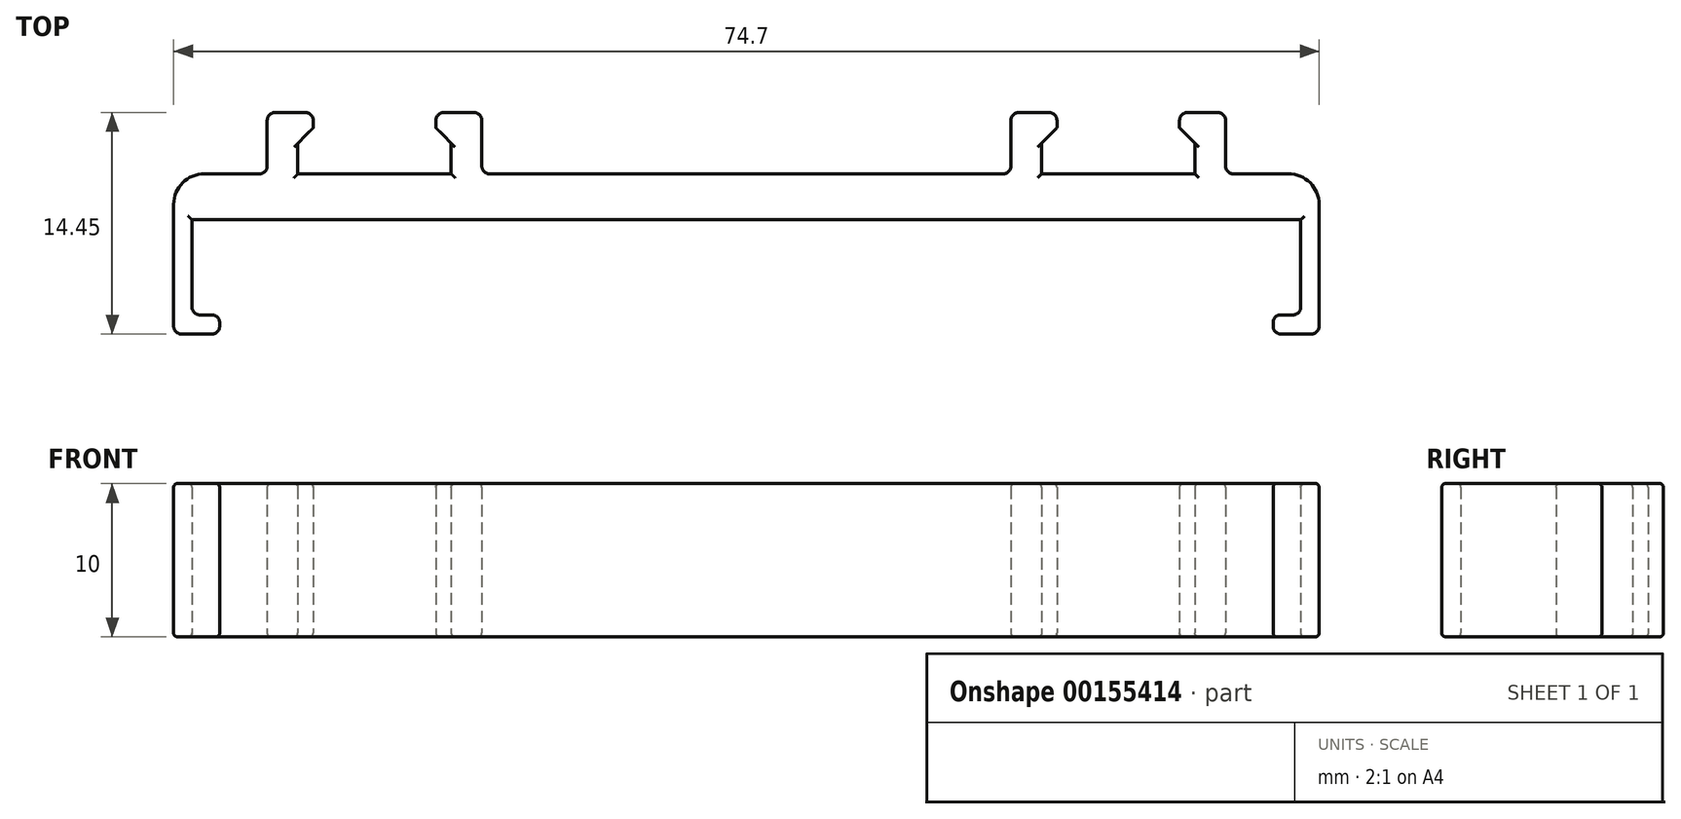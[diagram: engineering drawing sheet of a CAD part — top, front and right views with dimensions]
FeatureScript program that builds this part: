
annotation { "Feature Type Name" : "Feature", "Feature Type Description" : "" }
export const myFeature = defineFeature(function(context is Context, id is Id, definition is map)
    precondition{}
    {
        {
            var Q0;
            Q0=qCreatedBy(makeId("Top.planeOp"),FACE);
            var sketch = newSketch(context, id + "F0", { "sketchPlane" : qUnion([Q0])});
            skLineSegment(sketch, "E0.bottom", {"start": v(-35.35, 3) * mm, "end": v(-31.75, 3) * mm});
            skLineSegment(sketch, "E0.top", {"start": v(-36.15, 0) * mm, "end": v(0, 0) * mm});
            skLineSegment(sketch, "E0.left", {"start": v(-37.35, 1) * mm, "end": v(-37.35, -6.95) * mm});
            skLineSegment(sketch, "E0.right", {"start": v(0, 3) * mm, "end": v(0, 0) * mm});
            skLineSegment(sketch, "E1", {"start": v(-36.85, -7.45) * mm, "end": v(-34.85, -7.45) * mm});
            skLineSegment(sketch, "E2", {"start": v(-31.25, 3.5) * mm, "end": v(-31.25, 6.5) * mm});
            skLineSegment(sketch, "E3", {"start": v(-29.25, 5) * mm, "end": v(-29.25, 3) * mm});
            skLineSegment(sketch, "E4", {"start": v(-19.25, 3) * mm, "end": v(-19.25, 5) * mm});
            skLineSegment(sketch, "E5", {"start": v(-17.25, 6.5) * mm, "end": v(-17.25, 3.5) * mm});
            skLineSegment(sketch, "E6.trimOffspring", {"start": v(-29.25, 3) * mm, "end": v(-19.25, 3) * mm});
            skLineSegment(sketch, "E7.trimOffspring", {"start": v(-16.75, 3) * mm, "end": v(0, 3) * mm});
            skLineSegment(sketch, "E8", {"start": v(-30.75, 7) * mm, "end": v(-28.75, 7) * mm});
            skLineSegment(sketch, "E9", {"start": v(-28.25, 6.5) * mm, "end": v(-28.25, 6) * mm});
            skLineSegment(sketch, "E10", {"start": v(-19.75, 7) * mm, "end": v(-17.75, 7) * mm});
            skPoint(sketch, "E11.visualSharp", {"position": v(-37.35, 3) * mm});
            skArc(sketch, "E11.filletArc", {"start": v(-35.35, 3) * mm, "mid": v(-36.76, 2.41) * mm, "end": v(-37.35, 1) * mm});
            skPoint(sketch, "E12.visualSharp", {"position": v(-37.35, -7.45) * mm});
            skArc(sketch, "E12.filletArc", {"start": v(-37.35, -6.95) * mm, "mid": v(-37.2, -7.3) * mm, "end": v(-36.85, -7.45) * mm});
            skArc(sketch, "E13.filletArc", {"start": v(-28.25, 6.5) * mm, "mid": v(-28.4, 6.85) * mm, "end": v(-28.75, 7) * mm});
            skPoint(sketch, "E14.visualSharp", {"position": v(-31.25, 7) * mm});
            skArc(sketch, "E14.filletArc", {"start": v(-30.75, 7) * mm, "mid": v(-31.1, 6.85) * mm, "end": v(-31.25, 6.5) * mm});
            skArc(sketch, "E15.filletArc", {"start": v(-17.25, 6.5) * mm, "mid": v(-17.4, 6.85) * mm, "end": v(-17.75, 7) * mm});
            skArc(sketch, "E16.filletArc", {"start": v(-19.75, 7) * mm, "mid": v(-20.1, 6.85) * mm, "end": v(-20.25, 6.5) * mm});
            skPoint(sketch, "E17.visualSharp", {"position": v(-31.25, 3) * mm});
            skArc(sketch, "E17.filletArc", {"start": v(-31.75, 3) * mm, "mid": v(-31.4, 3.15) * mm, "end": v(-31.25, 3.5) * mm});
            skPoint(sketch, "E18.visualSharp", {"position": v(-17.25, 3) * mm});
            skArc(sketch, "E18.filletArc", {"start": v(-17.25, 3.5) * mm, "mid": v(-17.1, 3.15) * mm, "end": v(-16.75, 3) * mm});
            skLineSegment(sketch, "E19", {"start": v(-34.35, -6.95) * mm, "end": v(-34.35, -6.7) * mm});
            skLineSegment(sketch, "E20", {"start": v(-34.85, -6.2) * mm, "end": v(-35.65, -6.2) * mm});
            skLineSegment(sketch, "E21", {"start": v(-36.15, -5.7) * mm, "end": v(-36.15, 0) * mm});
            skPoint(sketch, "E22.visualSharp", {"position": v(-34.35, -7.45) * mm});
            skArc(sketch, "E22.filletArc", {"start": v(-34.85, -7.45) * mm, "mid": v(-34.5, -7.3) * mm, "end": v(-34.35, -6.95) * mm});
            skPoint(sketch, "E23.visualSharp", {"position": v(-34.35, -6.2) * mm});
            skArc(sketch, "E23.filletArc", {"start": v(-34.35, -6.7) * mm, "mid": v(-34.5, -6.35) * mm, "end": v(-34.85, -6.2) * mm});
            skPoint(sketch, "E24.visualSharp", {"position": v(-36.15, -6.2) * mm});
            skArc(sketch, "E24.filletArc", {"start": v(-36.15, -5.7) * mm, "mid": v(-36, -6.05) * mm, "end": v(-35.65, -6.2) * mm});
            skLineSegment(sketch, "E25", {"start": v(-29.25, 5) * mm, "end": v(-28.25, 6) * mm});
            skLineSegment(sketch, "E26", {"start": v(-29.25, 5) * mm, "end": v(-26.76, 5) * mm, "construction": true});
            skLineSegment(sketch, "E27", {"start": v(-20.25, 6.5) * mm, "end": v(-20.25, 6) * mm});
            skLineSegment(sketch, "E28", {"start": v(-20.25, 6) * mm, "end": v(-19.25, 5) * mm});
            skLineSegment(sketch, "E29", {"start": v(-19.25, 5) * mm, "end": v(-20.65, 5) * mm, "construction": true});
            skSolve(sketch);
        }
        {
            var Q0;
            Q0 = qSketchRegion(id + "F0", true);
            extrude(context, id + "F1", {"entities" : qUnion([Q0]), "depth" : 5 * mm});
        }
        {
            var Q0;
            Q0=makeQuery(id+"F1.opExtrude","CAP_EDGE",EDGE,{"disambiguationData":[OSD([sQuery(id+"F0.wireOp",EDGE,"E0.left")])],"isStart":false});
            var Q1;
            Q1=makeQuery(id+"F1.opExtrude","CAP_EDGE",EDGE,{"disambiguationData":[OSD([sQuery(id+"F0.wireOp",EDGE,"tvZSsmSE-hUvE-Xtk3-tDF4-9MUb7sZ0VrVc")])],"isStart":false});
            var Q2;
            Q2=makeQuery(id+"F1.opExtrude","CAP_EDGE",EDGE,{"disambiguationData":[OSD([sQuery(id+"F0.wireOp",EDGE,"E0.top")])],"isStart":false});
            var Q3;
            Q3=makeQuery(id+"F1.opExtrude","CAP_EDGE",EDGE,{"disambiguationData":[OSD([sQuery(id+"F0.wireOp",EDGE,"E7.trimOffspring")])],"isStart":false});
            var Q4;
            Q4=makeQuery(id+"F1.opExtrude","CAP_EDGE",EDGE,{"disambiguationData":[OSD([sQuery(id+"F0.wireOp",EDGE,"X6ObSeEj-YZr1-teH5-AZXu-cSIaNaP9HJV4")])],"isStart":false});
            var Q5;
            Q5=makeQuery(id+"F1.opExtrude","CAP_EDGE",EDGE,{"disambiguationData":[OSD([sQuery(id+"F0.wireOp",EDGE,"E4")])],"isStart":false});
            var Q6;
            Q6=makeQuery(id+"F1.opExtrude","CAP_EDGE",EDGE,{"disambiguationData":[OSD([sQuery(id+"F0.wireOp",EDGE,"E6.trimOffspring")])],"isStart":false});
            var Q7;
            Q7=makeQuery(id+"F1.opExtrude","CAP_EDGE",EDGE,{"disambiguationData":[OSD([sQuery(id+"F0.wireOp",EDGE,"E3")])],"isStart":false});
            var Q8;
            Q8=makeQuery(id+"F1.opExtrude","CAP_EDGE",EDGE,{"disambiguationData":[OSD([sQuery(id+"F0.wireOp",EDGE,"p37QHmaa-qxUZ-rcvS-T9Jj-RTMhVuBpOhlm")])],"isStart":false});
            fillet(context, id + "F2", {"entities" : qUnion([Q0, Q1, Q2, Q3, Q4, Q5, Q6, Q7, Q8]), "radius" : 0.25 * mm, "tangentPropagation" : true, "allowEdgeOverflow" : false});
        }
        {
            var Q0;
            Q0=makeQuery(id+"F1.opExtrude","SWEPT_BODY",BODY,{"disambiguationData":[OSD([sQuery(id+"F0.wireOp",EDGE,"E0.bottom"),sQuery(id+"F0.wireOp",EDGE,"E0.top"),sQuery(id+"F0.wireOp",EDGE,"E0.left"),sQuery(id+"F0.wireOp",EDGE,"E0.right"),sQuery(id+"F0.wireOp",EDGE,"E1"),sQuery(id+"F0.wireOp",EDGE,"hb15ITHf-txwg-p7V1-AkCO-Q5CLrczJ6zII"),sQuery(id+"F0.wireOp",EDGE,"Mp94Wzwl-Bjus-MnSt-C4gq-dxj1KtEF7oJ2"),sQuery(id+"F0.wireOp",EDGE,"tvZSsmSE-hUvE-Xtk3-tDF4-9MUb7sZ0VrVc"),sQuery(id+"F0.wireOp",EDGE,"E2"),sQuery(id+"F0.wireOp",EDGE,"p37QHmaa-qxUZ-rcvS-T9Jj-RTMhVuBpOhlm"),sQuery(id+"F0.wireOp",EDGE,"E3"),sQuery(id+"F0.wireOp",EDGE,"E4"),sQuery(id+"F0.wireOp",EDGE,"X6ObSeEj-YZr1-teH5-AZXu-cSIaNaP9HJV4"),sQuery(id+"F0.wireOp",EDGE,"E5"),sQuery(id+"F0.wireOp",EDGE,"E6.trimOffspring"),sQuery(id+"F0.wireOp",EDGE,"E7.trimOffspring"),sQuery(id+"F0.wireOp",EDGE,"E8"),sQuery(id+"F0.wireOp",EDGE,"E9"),sQuery(id+"F0.wireOp",EDGE,"iGBChI1A-pXvF-3BVJ-ZSPA-OomGo4UHPv9J"),sQuery(id+"F0.wireOp",EDGE,"E10"),sQuery(id+"F0.wireOp",EDGE,"E11.filletArc"),sQuery(id+"F0.wireOp",EDGE,"E12.filletArc"),sQuery(id+"F0.wireOp",EDGE,"12ba19c6-ba22-42b2-8e6c-7051c873ee4f.filletArc"),sQuery(id+"F0.wireOp",EDGE,"d1683e4d-4b4b-44b7-85b4-7357f9d20dbb.filletArc"),sQuery(id+"F0.wireOp",EDGE,"E13.filletArc"),sQuery(id+"F0.wireOp",EDGE,"E14.filletArc"),sQuery(id+"F0.wireOp",EDGE,"E15.filletArc"),sQuery(id+"F0.wireOp",EDGE,"E16.filletArc"),sQuery(id+"F0.wireOp",EDGE,"E17.filletArc"),sQuery(id+"F0.wireOp",EDGE,"E18.filletArc")])]});
            var Q1;
            Q1=makeQuery(id+"F1.opExtrude","CAP_FACE",FACE,{"disambiguationData":[OSD([sQuery(id+"F0.wireOp",EDGE,"E0.bottom"),sQuery(id+"F0.wireOp",EDGE,"E0.top"),sQuery(id+"F0.wireOp",EDGE,"E0.left"),sQuery(id+"F0.wireOp",EDGE,"E0.right"),sQuery(id+"F0.wireOp",EDGE,"E1"),sQuery(id+"F0.wireOp",EDGE,"hb15ITHf-txwg-p7V1-AkCO-Q5CLrczJ6zII"),sQuery(id+"F0.wireOp",EDGE,"Mp94Wzwl-Bjus-MnSt-C4gq-dxj1KtEF7oJ2"),sQuery(id+"F0.wireOp",EDGE,"tvZSsmSE-hUvE-Xtk3-tDF4-9MUb7sZ0VrVc"),sQuery(id+"F0.wireOp",EDGE,"E2"),sQuery(id+"F0.wireOp",EDGE,"p37QHmaa-qxUZ-rcvS-T9Jj-RTMhVuBpOhlm"),sQuery(id+"F0.wireOp",EDGE,"E3"),sQuery(id+"F0.wireOp",EDGE,"E4"),sQuery(id+"F0.wireOp",EDGE,"X6ObSeEj-YZr1-teH5-AZXu-cSIaNaP9HJV4"),sQuery(id+"F0.wireOp",EDGE,"E5"),sQuery(id+"F0.wireOp",EDGE,"E6.trimOffspring"),sQuery(id+"F0.wireOp",EDGE,"E7.trimOffspring"),sQuery(id+"F0.wireOp",EDGE,"E8"),sQuery(id+"F0.wireOp",EDGE,"E9"),sQuery(id+"F0.wireOp",EDGE,"iGBChI1A-pXvF-3BVJ-ZSPA-OomGo4UHPv9J"),sQuery(id+"F0.wireOp",EDGE,"E10"),sQuery(id+"F0.wireOp",EDGE,"E11.filletArc"),sQuery(id+"F0.wireOp",EDGE,"E12.filletArc"),sQuery(id+"F0.wireOp",EDGE,"12ba19c6-ba22-42b2-8e6c-7051c873ee4f.filletArc"),sQuery(id+"F0.wireOp",EDGE,"d1683e4d-4b4b-44b7-85b4-7357f9d20dbb.filletArc"),sQuery(id+"F0.wireOp",EDGE,"E13.filletArc"),sQuery(id+"F0.wireOp",EDGE,"E14.filletArc"),sQuery(id+"F0.wireOp",EDGE,"E15.filletArc"),sQuery(id+"F0.wireOp",EDGE,"E16.filletArc"),sQuery(id+"F0.wireOp",EDGE,"E17.filletArc"),sQuery(id+"F0.wireOp",EDGE,"E18.filletArc")])],"isStart":true});
            mirror(context, id + "F3", {"operationType" : NewBodyOperationType.ADD, "entities" : qUnion([Q0]), "mirrorPlane" : qUnion([Q1])});
        }
        {
            var Q0;
            Q0=makeQuery(id+"F1.opExtrude","SWEPT_BODY",BODY,{"disambiguationData":[OSD([sQuery(id+"F0.wireOp",EDGE,"E0.bottom"),sQuery(id+"F0.wireOp",EDGE,"E0.top"),sQuery(id+"F0.wireOp",EDGE,"E0.left"),sQuery(id+"F0.wireOp",EDGE,"E0.right"),sQuery(id+"F0.wireOp",EDGE,"E1"),sQuery(id+"F0.wireOp",EDGE,"hb15ITHf-txwg-p7V1-AkCO-Q5CLrczJ6zII"),sQuery(id+"F0.wireOp",EDGE,"Mp94Wzwl-Bjus-MnSt-C4gq-dxj1KtEF7oJ2"),sQuery(id+"F0.wireOp",EDGE,"tvZSsmSE-hUvE-Xtk3-tDF4-9MUb7sZ0VrVc"),sQuery(id+"F0.wireOp",EDGE,"E2"),sQuery(id+"F0.wireOp",EDGE,"p37QHmaa-qxUZ-rcvS-T9Jj-RTMhVuBpOhlm"),sQuery(id+"F0.wireOp",EDGE,"E3"),sQuery(id+"F0.wireOp",EDGE,"E4"),sQuery(id+"F0.wireOp",EDGE,"X6ObSeEj-YZr1-teH5-AZXu-cSIaNaP9HJV4"),sQuery(id+"F0.wireOp",EDGE,"E5"),sQuery(id+"F0.wireOp",EDGE,"E6.trimOffspring"),sQuery(id+"F0.wireOp",EDGE,"E7.trimOffspring"),sQuery(id+"F0.wireOp",EDGE,"E8"),sQuery(id+"F0.wireOp",EDGE,"E9"),sQuery(id+"F0.wireOp",EDGE,"iGBChI1A-pXvF-3BVJ-ZSPA-OomGo4UHPv9J"),sQuery(id+"F0.wireOp",EDGE,"E10"),sQuery(id+"F0.wireOp",EDGE,"E11.filletArc"),sQuery(id+"F0.wireOp",EDGE,"E12.filletArc"),sQuery(id+"F0.wireOp",EDGE,"12ba19c6-ba22-42b2-8e6c-7051c873ee4f.filletArc"),sQuery(id+"F0.wireOp",EDGE,"d1683e4d-4b4b-44b7-85b4-7357f9d20dbb.filletArc"),sQuery(id+"F0.wireOp",EDGE,"E13.filletArc"),sQuery(id+"F0.wireOp",EDGE,"E14.filletArc"),sQuery(id+"F0.wireOp",EDGE,"E15.filletArc"),sQuery(id+"F0.wireOp",EDGE,"E16.filletArc"),sQuery(id+"F0.wireOp",EDGE,"E17.filletArc"),sQuery(id+"F0.wireOp",EDGE,"E18.filletArc")])]});
            var Q1;
            {var subQ0=makeQuery(id+"F1.opExtrude","SWEPT_FACE",FACE,{"disambiguationData":[OSD([sQuery(id+"F0.wireOp",EDGE,"E0.right")])]});Q1=makeQuery(id+"F3.boolean.opBoolean","MERGE",FACE,{"derivedFrom":[subQ0,makeQuery(id+"F3.opPattern","COPY",FACE,{"derivedFrom":subQ0,"instanceName":"1"})]});}
            mirror(context, id + "F4", {"operationType" : NewBodyOperationType.ADD, "entities" : qUnion([Q0]), "mirrorPlane" : qUnion([Q1])});
        }
    });
